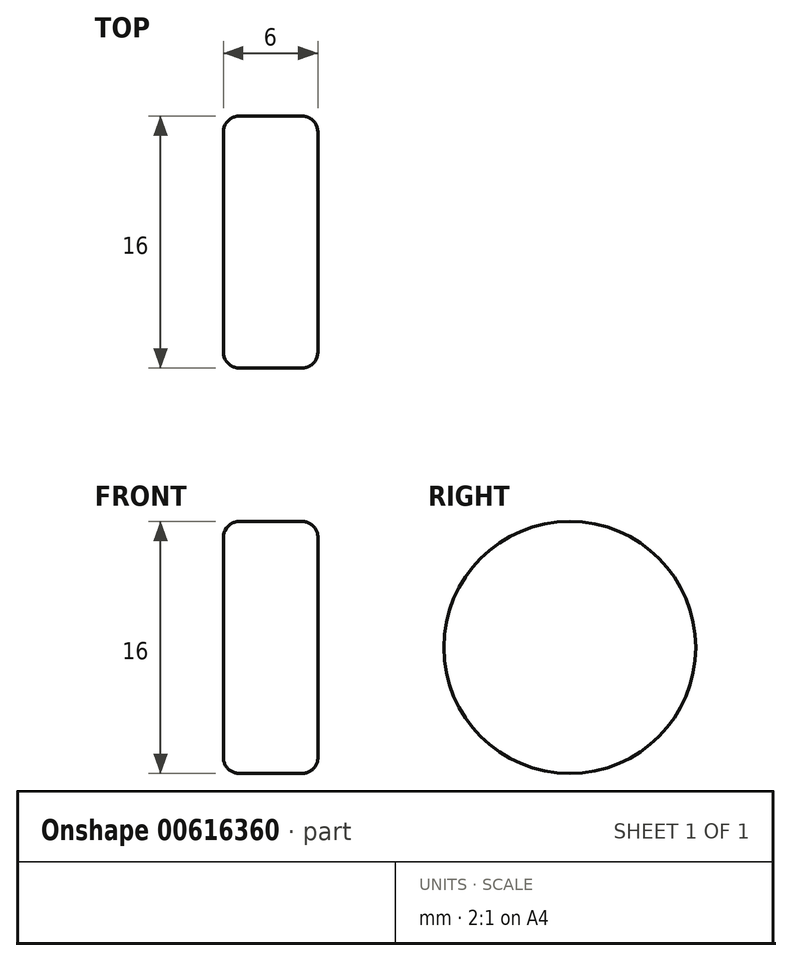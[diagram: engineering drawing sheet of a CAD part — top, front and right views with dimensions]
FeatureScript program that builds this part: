
annotation { "Feature Type Name" : "Feature", "Feature Type Description" : "" }
export const myFeature = defineFeature(function(context is Context, id is Id, definition is map)
    precondition{}
    {
        {
            var Q0;
            Q0=qCreatedBy(makeId("Right.planeOp"),FACE);
            var sketch = newSketch(context, id + "F0", { "sketchPlane" : qUnion([Q0])});
            skCircle(sketch, "E0", {"center": v(0, 0) * mm, "radius": 8 * mm});
            skSolve(sketch);
        }
        {
            var Q0;
            Q0 = qSketchRegion(id + "F0", true);
            extrude(context, id + "F1", {"entities" : qUnion([Q0]), "depth" : 6 * mm, "offsetDistance" : 25 * mm});
        }
        {
            var Q0;
            Q0=makeQuery(id+"F1.opExtrude","CAP_EDGE",EDGE,{"disambiguationData":[OSD([sQuery(id+"F0.wireOp",EDGE,"E0")])],"isStart":true});
            var Q1;
            Q1=makeQuery(id+"F1.opExtrude","CAP_EDGE",EDGE,{"disambiguationData":[OSD([sQuery(id+"F0.wireOp",EDGE,"E0")])],"isStart":false});
            fillet(context, id + "F2", {"entities" : qUnion([Q0, Q1]), "radius" : 1 * mm, "tangentPropagation" : true, "allowEdgeOverflow" : false});
        }
    });
